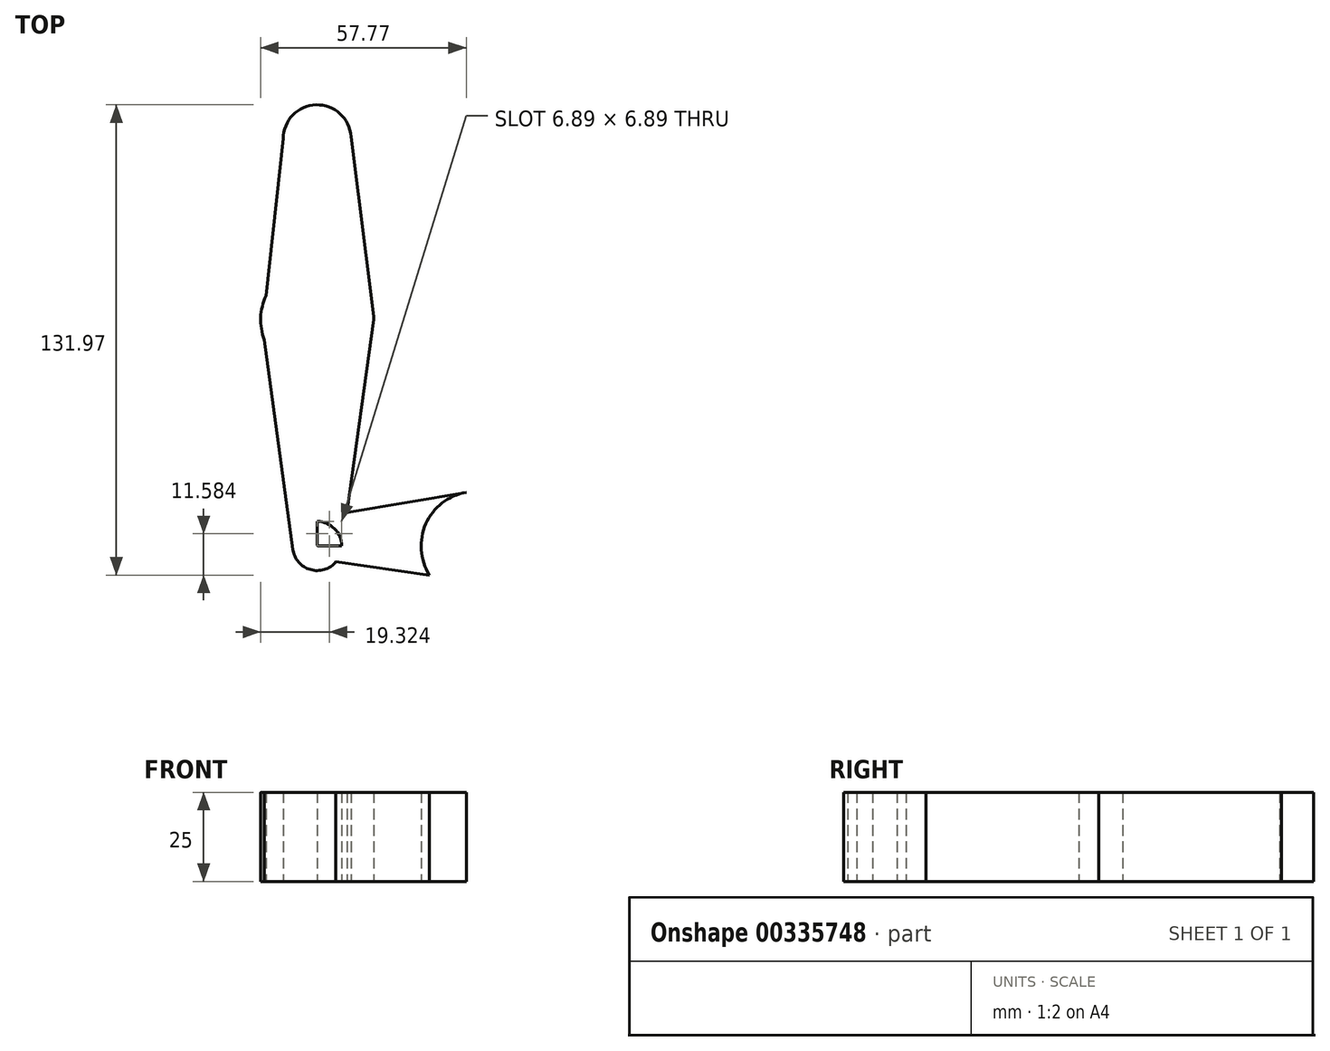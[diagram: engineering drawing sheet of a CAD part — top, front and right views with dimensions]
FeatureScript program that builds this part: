
annotation { "Feature Type Name" : "Feature", "Feature Type Description" : "" }
export const myFeature = defineFeature(function(context is Context, id is Id, definition is map)
    precondition{}
    {
        {
            var Q0;
            Q0=qCreatedBy(makeId("Top.planeOp"),FACE);
            var sketch = newSketch(context, id + "F0", { "sketchPlane" : qUnion([Q0])});
            skLineSegment(sketch, "E0", {"start": v(0, 0.3) * mm, "end": v(0, 114.3) * mm});
            skCircle(sketch, "E1", {"center": v(0, 0) * mm, "radius": 6.89 * mm});
            skCircle(sketch, "E2", {"center": v(0, 114.3) * mm, "radius": 9.53 * mm});
            skCircle(sketch, "E3", {"center": v(0, 63.5) * mm, "radius": 15.88 * mm});
            skLineSegment(sketch, "E4", {"start": v(0.3, 0) * mm, "end": v(60.33, 0) * mm});
            skCircle(sketch, "E5", {"center": v(44.45, 0) * mm, "radius": 15.27 * mm});
            skLineSegment(sketch, "E6", {"start": v(15.88, 63.5) * mm, "end": v(8.32, 9.74) * mm});
            skLineSegment(sketch, "E7", {"start": v(9.5, 114.91) * mm, "end": v(15.75, 65.49) * mm});
            skLineSegment(sketch, "E8", {"start": v(41.89, 15.06) * mm, "end": v(8.67, 9.4) * mm});
            skLineSegment(sketch, "E9", {"start": v(43.42, -9.81) * mm, "end": v(5.26, -4.45) * mm});
            skLineSegment(sketch, "E10", {"start": v(-9.53, 114.3) * mm, "end": v(-14.36, 70.26) * mm});
            skLineSegment(sketch, "E11", {"start": v(-14.85, 57.9) * mm, "end": v(-6.82, -0.93) * mm});
            skPoint(sketch, "E12.newPointB", {"position": v(6.96, 0) * mm});
            skArc(sketch, "E12.filletArc", {"start": v(8.32, 9.74) * mm, "mid": v(8.41, 9.49) * mm, "end": v(8.67, 9.4) * mm});
            skArc(sketch, "E13.filletArc", {"start": v(0, 0.3) * mm, "mid": v(0.09, 0.09) * mm, "end": v(0.3, 0) * mm});
            skSolve(sketch);
        }
        {
            var Q0;
            {var subQ5=sQuery(id+"F0.wireOp",EDGE,"E11");Q0=makeQuery(id+"F0.imprint","IMPRINT",FACE,{"disambiguationData":[TD([[makeQuery(id+"F0.imprint","IMPRINT",EDGE,{"derivedFrom":subQ5}),1.0]])]});}
            var Q1;
            {var subQ12=sQuery(id+"F0.wireOp",EDGE,"E8");Q1=makeQuery(id+"F0.imprint","IMPRINT",FACE,{"disambiguationData":[TD([[makeQuery(id+"F0.imprint","IMPRINT",EDGE,{"derivedFrom":subQ12}),1.0]])]});}
            var Q2;
            {var subQ0=sQuery(id+"F0.wireOp",EDGE,"E5");var subQ1=sQuery(id+"F0.wireOp",EDGE,"E4");var subQ2=makeQuery(id+"F0.imprint","INTERSECT",VERTEX,{"disambiguationData":[OD(0.0)],"derivedFrom":[subQ1,subQ0]});Q2=makeQuery(id+"F0.imprint","IMPRINT",FACE,{"disambiguationData":[TD([[makeQuery(id+"F0.imprint","IMPRINT",EDGE,{"disambiguationData":[TD([[subQ2,1.0]])],"derivedFrom":subQ1}),-1.0]])]});}
            var Q3;
            {var subQ0=sQuery(id+"F0.wireOp",EDGE,"E9");var subQ1=sQuery(id+"F0.wireOp",EDGE,"E1");var subQ2=makeQuery(id+"F0.imprint","INTERSECT",VERTEX,{"derivedFrom":[subQ1,subQ0]});Q3=makeQuery(id+"F0.imprint","IMPRINT",FACE,{"disambiguationData":[TD([[makeQuery(id+"F0.imprint","IMPRINT",EDGE,{"disambiguationData":[TD([[subQ2,-1.0]])],"derivedFrom":subQ1}),-1.0]])]});}
            var Q4;
            {var subQ4=sQuery(id+"F0.wireOp",EDGE,"E13.filletArc");Q4=makeQuery(id+"F0.imprint","IMPRINT",FACE,{"disambiguationData":[TD([[makeQuery(id+"F0.imprint","IMPRINT",EDGE,{"derivedFrom":subQ4}),-1.0]])]});}
            var Q5;
            {var subQ5=sQuery(id+"F0.wireOp",EDGE,"E10");Q5=makeQuery(id+"F0.imprint","IMPRINT",FACE,{"disambiguationData":[TD([[makeQuery(id+"F0.imprint","IMPRINT",EDGE,{"derivedFrom":subQ5}),1.0]])]});}
            var Q6;
            {var subQ0=sQuery(id+"F0.wireOp",EDGE,"E2");var subQ1=makeQuery(id+"F0.imprint","INTERSECT",VERTEX,{"derivedFrom":[subQ0,sQuery(id+"F0.wireOp",EDGE,"E7")]});Q6=makeQuery(id+"F0.imprint","IMPRINT",FACE,{"disambiguationData":[TD([[makeQuery(id+"F0.imprint","IMPRINT",EDGE,{"disambiguationData":[TD([[subQ1,-1.0]])],"derivedFrom":subQ0}),1.0]])]});}
            var Q7;
            {var subQ0=sQuery(id+"F0.wireOp",EDGE,"E5");var subQ1=sQuery(id+"F0.wireOp",EDGE,"E4");var subQ2=makeQuery(id+"F0.imprint","INTERSECT",VERTEX,{"disambiguationData":[OD(0.0)],"derivedFrom":[subQ1,subQ0]});Q7=makeQuery(id+"F0.imprint","IMPRINT",FACE,{"disambiguationData":[TD([[makeQuery(id+"F0.imprint","IMPRINT",EDGE,{"disambiguationData":[TD([[subQ2,1.0]])],"derivedFrom":subQ1}),1.0]])]});}
            var Q8;
            {var subQ5=sQuery(id+"F0.wireOp",EDGE,"E7");Q8=makeQuery(id+"F0.imprint","IMPRINT",FACE,{"disambiguationData":[TD([[makeQuery(id+"F0.imprint","IMPRINT",EDGE,{"derivedFrom":subQ5}),-1.0]])]});}
            var Q9;
            {var subQ1=sQuery(id+"F0.wireOp",EDGE,"E3");var subQ3=sQuery(id+"F0.wireOp",EDGE,"E0");var subQ4=makeQuery(id+"F0.imprint","INTERSECT",VERTEX,{"disambiguationData":[OD(0.0)],"derivedFrom":[subQ3,subQ1]});Q9=makeQuery(id+"F0.imprint","IMPRINT",FACE,{"disambiguationData":[TD([[makeQuery(id+"F0.imprint","IMPRINT",EDGE,{"disambiguationData":[TD([[subQ4,-1.0]])],"derivedFrom":subQ3}),-1.0]])]});}
            var Q10;
            {var subQ0=sQuery(id+"F0.wireOp",EDGE,"E3");var subQ1=sQuery(id+"F0.wireOp",EDGE,"E0");var subQ2=makeQuery(id+"F0.imprint","INTERSECT",VERTEX,{"disambiguationData":[OD(0.0)],"derivedFrom":[subQ1,subQ0]});Q10=makeQuery(id+"F0.imprint","IMPRINT",FACE,{"disambiguationData":[TD([[makeQuery(id+"F0.imprint","IMPRINT",EDGE,{"disambiguationData":[TD([[subQ2,-1.0]])],"derivedFrom":subQ1}),1.0]])]});}
            extrude(context, id + "F1", {"entities" : qUnion([Q0, Q1, Q2, Q3, Q4, Q5, Q6, Q7, Q8, Q9, Q10]), "depth" : 25 * mm});
        }
    });
